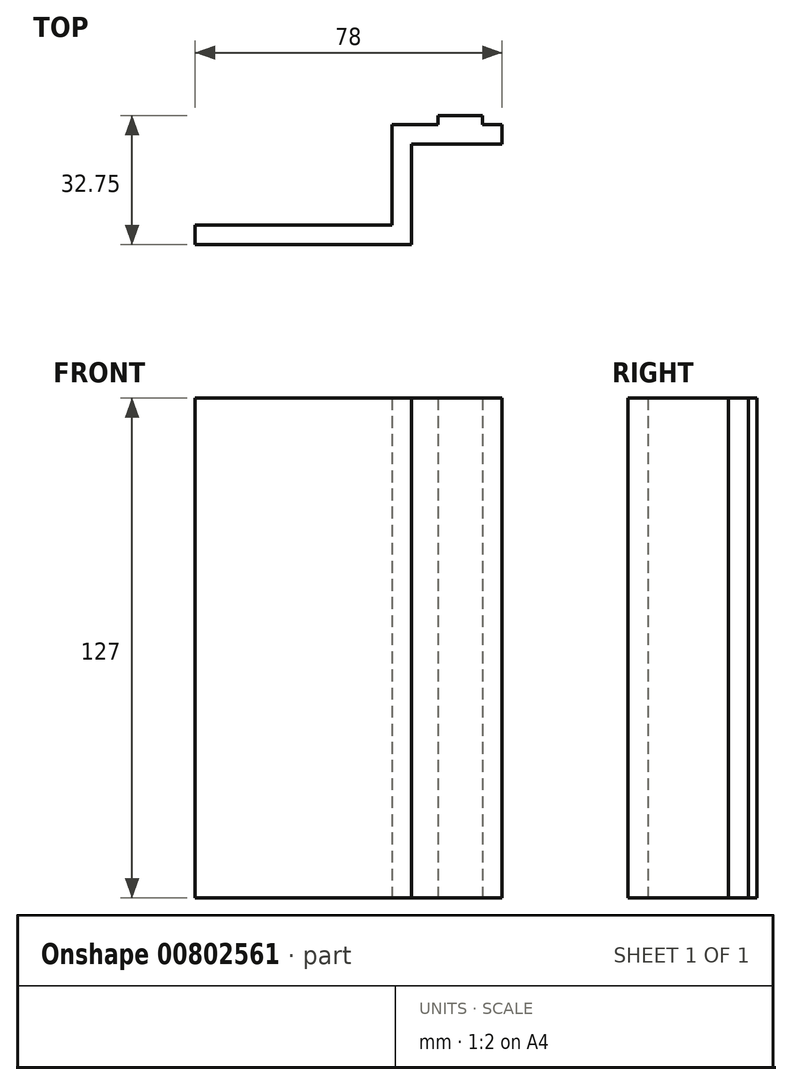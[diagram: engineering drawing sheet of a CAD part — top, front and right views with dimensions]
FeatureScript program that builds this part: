
annotation { "Feature Type Name" : "Feature", "Feature Type Description" : "" }
export const myFeature = defineFeature(function(context is Context, id is Id, definition is map)
    precondition{}
    {
        {
            var Q0;
            Q0=qCreatedBy(makeId("Top.planeOp"),FACE);
            var sketch = newSketch(context, id + "F0", { "sketchPlane" : qUnion([Q0])});
            skLineSegment(sketch, "E0.bottom", {"start": v(0, 0) * mm, "end": v(-50, 0) * mm});
            skLineSegment(sketch, "E0.top", {"start": v(0, -5) * mm, "end": v(-50, -5) * mm});
            skLineSegment(sketch, "E0.left", {"start": v(0, 0) * mm, "end": v(0, -5) * mm});
            skLineSegment(sketch, "E0.right", {"start": v(-50, 0) * mm, "end": v(-50, -5) * mm});
            skLineSegment(sketch, "E1.bottom", {"start": v(0, -5) * mm, "end": v(5, -5) * mm});
            skLineSegment(sketch, "E1.top", {"start": v(0, 25.5) * mm, "end": v(5, 25.5) * mm});
            skLineSegment(sketch, "E1.left", {"start": v(0, -5) * mm, "end": v(0, 25.5) * mm});
            skLineSegment(sketch, "E1.right", {"start": v(5, -5) * mm, "end": v(5, 25.5) * mm});
            skLineSegment(sketch, "E2.bottom", {"start": v(5, 25.5) * mm, "end": v(23, 25.5) * mm});
            skLineSegment(sketch, "E2.top", {"start": v(5, 20.5) * mm, "end": v(23, 20.5) * mm});
            skLineSegment(sketch, "E2.left", {"start": v(5, 25.5) * mm, "end": v(5, 20.5) * mm});
            skLineSegment(sketch, "E2.right", {"start": v(23, 25.5) * mm, "end": v(23, 20.5) * mm});
            skLineSegment(sketch, "E3.bottom", {"start": v(23, 25.5) * mm, "end": v(11.75, 25.5) * mm});
            skLineSegment(sketch, "E3.top", {"start": v(23, 27.75) * mm, "end": v(11.75, 27.75) * mm});
            skLineSegment(sketch, "E3.left", {"start": v(23, 25.5) * mm, "end": v(23, 27.75) * mm});
            skLineSegment(sketch, "E3.right", {"start": v(11.75, 25.5) * mm, "end": v(11.75, 27.75) * mm});
            skLineSegment(sketch, "E4.bottom", {"start": v(23, 20.5) * mm, "end": v(28, 20.5) * mm});
            skLineSegment(sketch, "E4.top", {"start": v(23, 25.5) * mm, "end": v(28, 25.5) * mm});
            skLineSegment(sketch, "E4.left", {"start": v(23, 20.5) * mm, "end": v(23, 25.5) * mm});
            skLineSegment(sketch, "E4.right", {"start": v(28, 20.5) * mm, "end": v(28, 25.5) * mm});
            skSolve(sketch);
        }
        {
            var Q0;
            Q0 = qSketchRegion(id + "F0", true);
            extrude(context, id + "F1", {"entities" : qUnion([Q0]), "depth" : 127 * mm, "offsetDistance" : 25.4 * mm});
        }
    });
